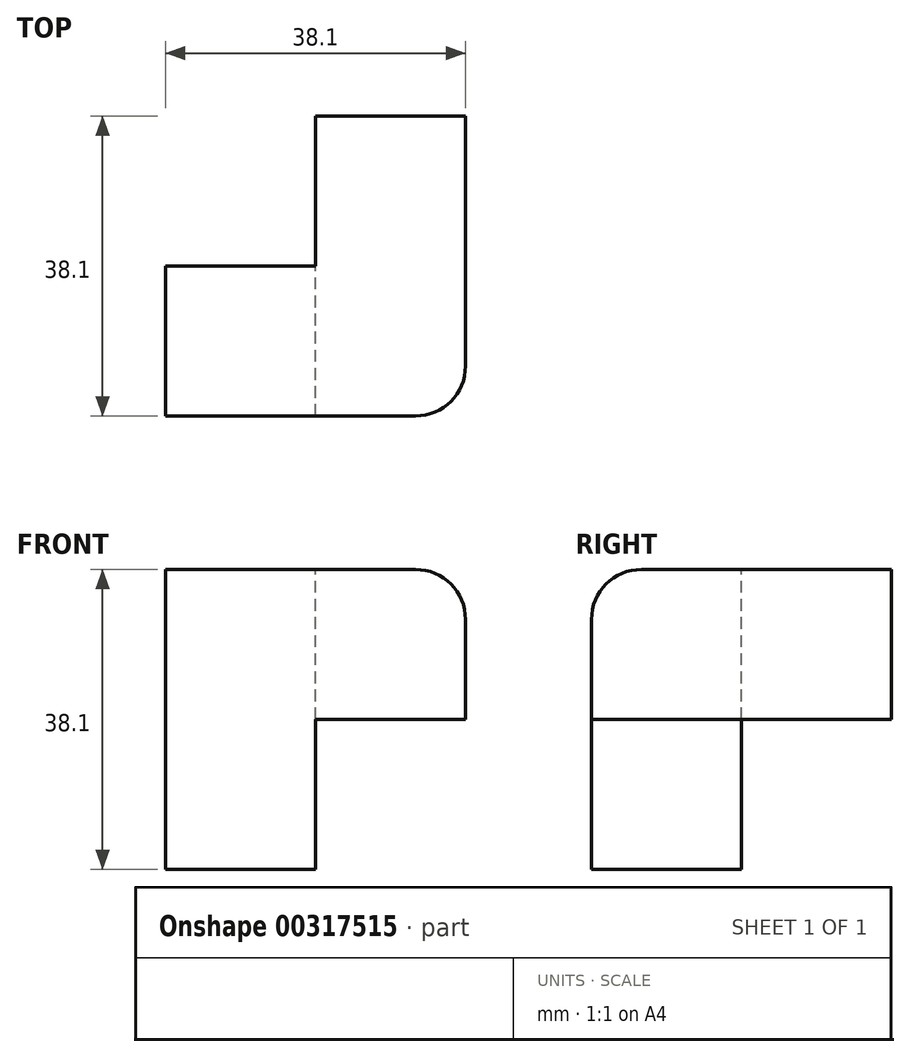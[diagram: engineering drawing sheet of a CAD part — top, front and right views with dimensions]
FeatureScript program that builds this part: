
annotation { "Feature Type Name" : "Feature", "Feature Type Description" : "" }
export const myFeature = defineFeature(function(context is Context, id is Id, definition is map)
    precondition{}
    {
        {
            var Q0;
            Q0=qCreatedBy(makeId("Front.planeOp"),FACE);
            var sketch = newSketch(context, id + "F0", { "sketchPlane" : qUnion([Q0])});
            skLineSegment(sketch, "E0.bottom", {"start": v(0, -2.29) * mm, "end": v(19.05, -2.29) * mm});
            skLineSegment(sketch, "E0.top", {"start": v(0, 35.81) * mm, "end": v(38.1, 35.81) * mm});
            skLineSegment(sketch, "E0.left", {"start": v(0, -2.29) * mm, "end": v(0, 35.81) * mm});
            skLineSegment(sketch, "E0.right", {"start": v(38.1, 16.76) * mm, "end": v(38.1, 35.81) * mm});
            skLineSegment(sketch, "E1.bottom", {"start": v(38.1, 16.76) * mm, "end": v(19.05, 16.76) * mm});
            skLineSegment(sketch, "E1.right", {"start": v(19.05, 16.76) * mm, "end": v(19.05, -2.29) * mm});
            skPoint(sketch, "E2.orphan", {"position": v(38.1, -2.29) * mm});
            skSolve(sketch);
        }
        {
            var Q0;
            Q0 = qSketchRegion(id + "F0", true);
            extrude(context, id + "F1", {"entities" : qUnion([Q0]), "depth" : 38.1 * mm});
        }
        {
            var Q0;
            Q0=makeQuery(id+"F1.opExtrude","SWEPT_FACE",FACE,{"disambiguationData":[OSD([sQuery(id+"F0.wireOp",EDGE,"E0.top")])]});
            var sketch = newSketch(context, id + "F2", { "sketchPlane" : qUnion([Q0])});
            skLineSegment(sketch, "E3.bottom", {"start": v(0, -19.05) * mm, "end": v(19.05, -19.05) * mm});
            skLineSegment(sketch, "E3.top", {"start": v(0, 0) * mm, "end": v(19.05, 0) * mm});
            skLineSegment(sketch, "E3.left", {"start": v(0, -19.05) * mm, "end": v(0, 0) * mm});
            skLineSegment(sketch, "E3.right", {"start": v(19.05, -19.05) * mm, "end": v(19.05, 0) * mm});
            skSolve(sketch);
        }
        {
            var Q0;
            Q0 = qSketchRegion(id + "F2", true);
            extrude(context, id + "F3", {"entities" : qUnion([Q0]), "operationType" : NewBodyOperationType.REMOVE, "endBound" : BoundingType.THROUGH_ALL, "oppositeDirection" : true, "depth" : 25.4 * mm});
        }
        {
            var Q0;
            Q0=makeQuery(id+"F1.opExtrude","CAP_EDGE",EDGE,{"disambiguationData":[OSD([sQuery(id+"F0.wireOp",EDGE,"E0.top")])],"isStart":false});
            fillet(context, id + "F4", {"entities" : qUnion([Q0]), "radius" : 6.35 * mm, "tangentPropagation" : true, "allowEdgeOverflow" : false});
        }
        {
            var Q0;
            Q0=makeQuery(id+"F1.opExtrude","SWEPT_EDGE",EDGE,{"disambiguationData":[OSD([sQuery(id+"F0.wireOp",EDGE,"E0.top"),sQuery(id+"F0.wireOp",EDGE,"E0.right")])]});
            fillet(context, id + "F5", {"entities" : qUnion([Q0]), "radius" : 6.35 * mm, "tangentPropagation" : true, "allowEdgeOverflow" : false});
        }
    });
